# Revit family: 02-60-0035 DN450-600 WITH BYPASS
name_source: partatom
category: Pipe Accessories
units: mm (PartAtom-declared; Revit-internal decimal feet)

## family parameters
Always vertical = Yes
Cut with Voids When Loaded = No
Part Type = Valve - Breaks Into
Round Connector Dimension = Use Diameter
Shared = No
Work Plane-Based = No

## types (6) — shared parameters
10 = 10 mm  [stored 0.0328084 ft]
3 = 3 mm  [stored 0.00984252 ft]
5 = 5 mm  [stored 0.0164042 ft]
BP_BH = 85 mm  [stored 0.278871 ft]
BP_BL = 50 mm  [stored 0.164042 ft]
BP_BW = 28 mm  [stored 0.0918635 ft]
BP_B_R = 30 mm  [stored 0.0984252 ft]
BP_FL_L. = 68 mm  [stored 0.223097 ft]
BP_FL_W = 35 mm  [stored 0.114829 ft]
BP_P_R = 55 mm  [stored 0.180446 ft]
BP_Pipe_dis = 83 mm
BP_Total_H = 208 mm
BP_stem = 9 mm  [stored 0.0295276 ft]
BP_stem_H = 36 mm  [stored 0.11811 ft]
BP_stem_R = 16 mm  [stored 0.0524934 ft]
Blind_P = 46 mm
Body_R = 34 mm
Body_T = 14 mm  [stored 0.0459318 ft]
Body_W = 136 mm
DN450_PN10 = 02-450-60-004642
DN450_PN16 = 02-450-60-014642
DN500_PN10 = 02-500-60-004642
DN500_PN16 = 02-500-60-014642
DN600_PN10 = 02-600-60-004642
DN600_PN16 = 02-600-60-014642
Description_ = AVK GATE VALVE, FLANGED, PN10/16
F = 15 mm  [stored 0.0492126 ft]
F14 = 88 mm
F2 = 70 mm  [stored 0.229659 ft]
Pipe_R = 31 mm
Rib_R = 81 mm
Search_table = 02-60-0035 DN450-600 WITH BYPASS
Stem_H = 91 mm  [stored 0.298556 ft]
URL_product_pages = https://www.avkvalves.com
Ww = 163 mm
zero-valued in all types: Default Elevation, F1

## per-type parameters (varying)
| type | BP_dis | Body_Arc | Body_H | Body_L | Bore_R | DN | Disk_T | FL_T | H | H3 | H3-H | L | OD | Raised_R | Raised_dis | Rib_H | Rib_T | W | W1 |
| DN600_PN10 | 607 mm | 195 mm  [stored 0.639764 ft] | 675 mm | 383 mm | 300 mm | 600 mm | 200 mm  [stored 0.656168 ft] | 30 mm  [stored 0.0984252 ft] | 1263 mm | 1682 mm | 419 mm | 800 mm | 390 mm | 341 mm | 5 mm  [stored 0.0164042 ft] | 169 mm | 15 mm  [stored 0.0492126 ft] | 479 mm | 251 mm |
| DN600_PN16 | 607 mm | 195 mm  [stored 0.639764 ft] | 675 mm | 383 mm | 300 mm | 600 mm | 200 mm  [stored 0.656168 ft] | 30 mm  [stored 0.0984252 ft] | 1263 mm | 1682 mm | 419 mm | 800 mm | 420 mm | 341 mm | 5 mm  [stored 0.0164042 ft] | 169 mm | 15 mm  [stored 0.0492126 ft] | 479 mm | 251 mm |
| DN500_PN10 | 557 mm | 163 mm | 580 mm | 336 mm | 250 mm | 500 mm | 175 mm  [stored 0.574147 ft] | 27 mm  [stored 0.0885827 ft] | 1124 mm | 1481 mm | 357 mm | 700 mm | 335 mm | 291 mm | 4 mm  [stored 0.0131234 ft] | 145 mm  [stored 0.475722 ft] | 14 mm  [stored 0.0459318 ft] | 420 mm | 214 mm |
| DN500_PN16 | 557 mm | 163 mm | 580 mm | 336 mm | 250 mm | 500 mm | 175 mm  [stored 0.574147 ft] | 32 mm  [stored 0.104987 ft] | 1124 mm | 1481 mm | 357 mm | 700 mm | 358 mm | 305 mm | 4 mm  [stored 0.0131234 ft] | 145 mm  [stored 0.475722 ft] | 16 mm  [stored 0.0524934 ft] | 420 mm | 214 mm |
| DN450_PN10 | 557 mm | 146 mm | 552 mm | 335 mm | 225 mm | 450 mm | 163 mm | 26 mm | 1096 mm | 1416 mm | 320 mm | 650 mm | 308 mm | 265 mm | 4 mm  [stored 0.0131234 ft] | 138 mm  [stored 0.452756 ft] | 13 mm | 419 mm | 192 mm |
| DN450_PN16 | 557 mm | 146 mm | 552 mm | 335 mm | 225 mm | 450 mm | 163 mm | 30 mm  [stored 0.0984252 ft] | 1096 mm | 1416 mm | 320 mm | 650 mm | 320 mm | 274 mm | 4 mm  [stored 0.0131234 ft] | 138 mm  [stored 0.452756 ft] | 15 mm  [stored 0.0492126 ft] | 419 mm | 192 mm |

note: [stored X ft] marks values corroborated as IEEE doubles in the binary element streams (Revit-internal decimal feet)

## geometry (parser evidence)
native form markers: Sweep x5
no freeform markers — native parametric forms only
